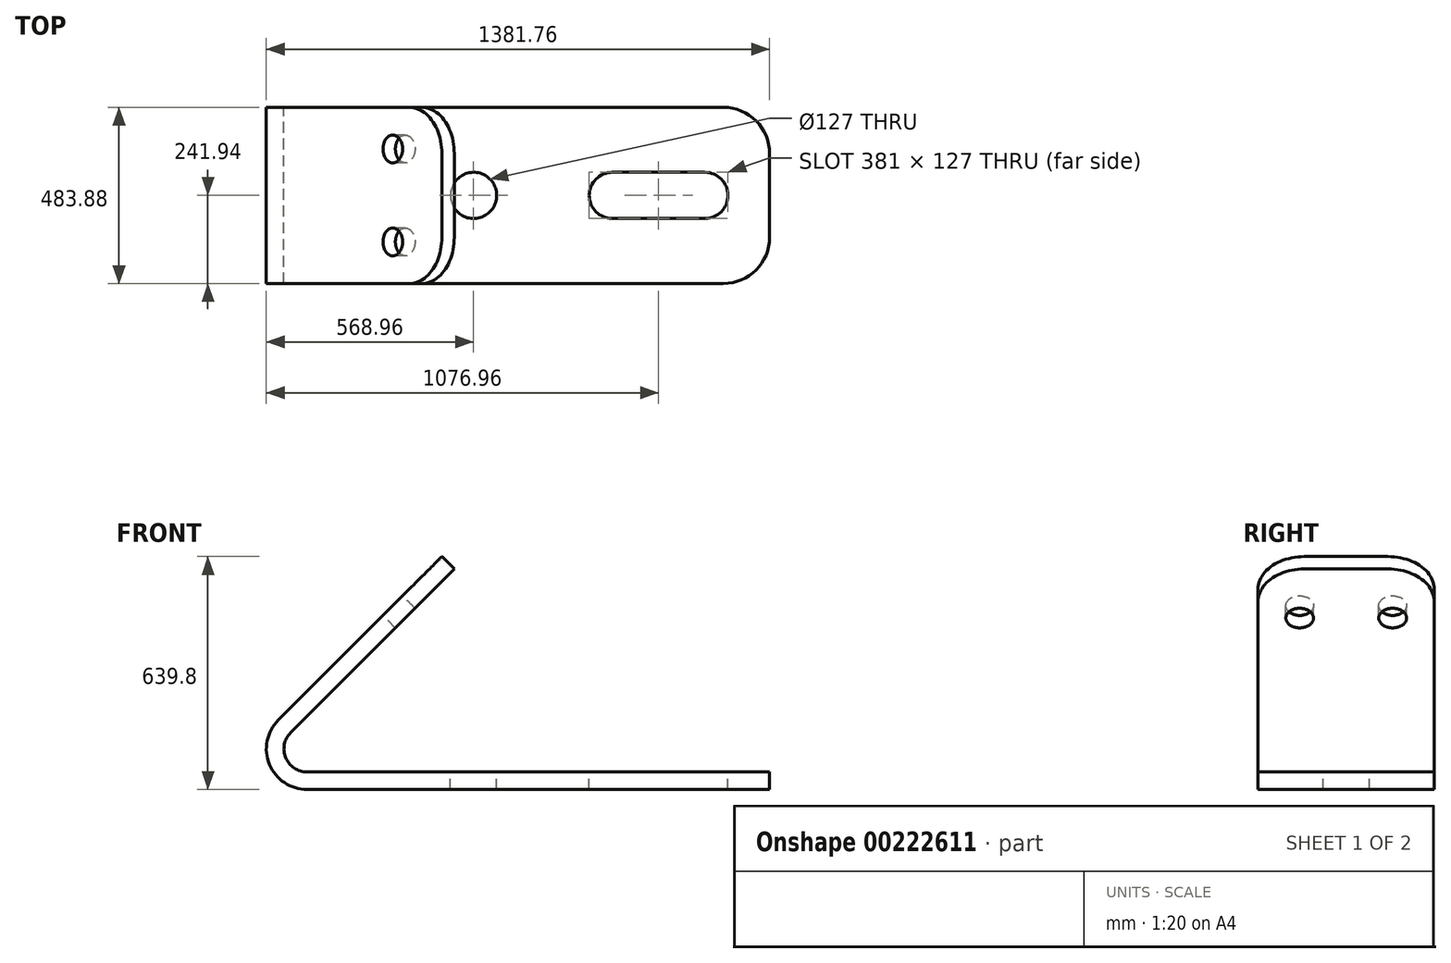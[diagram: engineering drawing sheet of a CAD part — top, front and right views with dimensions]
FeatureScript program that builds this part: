
annotation { "Feature Type Name" : "Feature", "Feature Type Description" : "" }
export const myFeature = defineFeature(function(context is Context, id is Id, definition is map)
    precondition{}
    {
        {
            var Q0;
            Q0=qCreatedBy(makeId("Front.planeOp"),FACE);
            var sketch = newSketch(context, id + "F0", { "sketchPlane" : qUnion([Q0])});
            skLineSegment(sketch, "E0", {"start": v(0, 0) * mm, "end": v(1270, 0) * mm});
            skLineSegment(sketch, "E1", {"start": v(1270, 0) * mm, "end": v(1270, 48.26) * mm});
            skLineSegment(sketch, "E2", {"start": v(369.99, 639.8) * mm, "end": v(-79.03, 190.79) * mm});
            skArc(sketch, "E3", {"start": v(-79.03, 190.79) * mm, "mid": v(-103.25, 69) * mm, "end": v(0, 0) * mm});
            skLineSegment(sketch, "E4", {"start": v(369.99, 639.8) * mm, "end": v(404.11, 605.67) * mm});
            skLineSegment(sketch, "E5", {"start": v(404.11, 605.67) * mm, "end": v(-44.9, 156.66) * mm});
            skLineSegment(sketch, "E6", {"start": v(1270, 48.26) * mm, "end": v(0, 48.26) * mm});
            skArc(sketch, "E7", {"start": v(0, 48.26) * mm, "mid": v(-58.67, 87.46) * mm, "end": v(-44.9, 156.66) * mm});
            skSolve(sketch);
        }
        {
            var Q0;
            Q0=makeQuery(id+"F0.imprint","IMPRINT",FACE,{"disambiguationData":[TD([[makeQuery(id+"F0.imprint","IMPRINT",EDGE,{"derivedFrom":sQuery(id+"F0.wireOp",EDGE,"E0")}),1.0]])]});
            extrude(context, id + "F1", {"entities" : qUnion([Q0]), "endBound" : BoundingType.SYMMETRIC, "depth" : 483.87 * mm});
        }
        {
            var Q0;
            Q0=makeQuery(id+"F1.opExtrude","SWEPT_FACE",FACE,{"disambiguationData":[OSD([sQuery(id+"F0.wireOp",EDGE,"E2")])]});
            var sketch = newSketch(context, id + "F2", { "sketchPlane" : qUnion([Q0])});
            skCircle(sketch, "E8", {"center": v(-127.64, 523.53) * mm, "radius": 38.1 * mm});
            skCircle(sketch, "E9", {"center": v(127.64, 523.53) * mm, "radius": 38.1 * mm});
            skSolve(sketch);
        }
        {
            var Q0;
            Q0 = qSketchRegion(id + "F2", true);
            extrude(context, id + "F3", {"entities" : qUnion([Q0]), "operationType" : NewBodyOperationType.REMOVE, "endBound" : BoundingType.UP_TO_NEXT, "oppositeDirection" : true, "depth" : 25.4 * mm});
        }
        {
            var Q0;
            Q0=makeQuery(id+"F1.opExtrude","SWEPT_FACE",FACE,{"disambiguationData":[OSD([sQuery(id+"F0.wireOp",EDGE,"E6")])]});
            var sketch = newSketch(context, id + "F4", { "sketchPlane" : qUnion([Q0])});
            skCircle(sketch, "E10", {"center": v(457.2, 0) * mm, "radius": 63.5 * mm});
            skLineSegment(sketch, "E11.bottom", {"start": v(1092.2, 63.5) * mm, "end": v(838.2, 63.5) * mm});
            skLineSegment(sketch, "E11.top", {"start": v(1092.2, -63.5) * mm, "end": v(838.2, -63.5) * mm});
            skPoint(sketch, "E11.middle", {"position": v(965.2, 0) * mm});
            skArc(sketch, "E12", {"start": v(838.2, 63.5) * mm, "mid": v(774.7, 0) * mm, "end": v(838.2, -63.5) * mm});
            skArc(sketch, "E13", {"start": v(1092.2, -63.5) * mm, "mid": v(1155.7, 0) * mm, "end": v(1092.2, 63.5) * mm});
            skPoint(sketch, "E13.centerSnap0", {"position": v(1155.7, 0) * mm});
            skPoint(sketch, "E14.orphan", {"position": v(774.7, 63.5) * mm});
            skPoint(sketch, "E15.orphan", {"position": v(774.7, -63.5) * mm});
            skPoint(sketch, "E16.orphan", {"position": v(1155.7, 63.5) * mm});
            skPoint(sketch, "E17.orphan", {"position": v(1155.7, -63.5) * mm});
            skSolve(sketch);
        }
        {
            var Q0;
            Q0 = qSketchRegion(id + "F4", true);
            extrude(context, id + "F5", {"entities" : qUnion([Q0]), "operationType" : NewBodyOperationType.REMOVE, "endBound" : BoundingType.THROUGH_ALL, "oppositeDirection" : true, "depth" : 25.4 * mm});
        }
        {
            var Q0;
            Q0=makeQuery(id+"F1.opExtrude","CAP_EDGE",EDGE,{"disambiguationData":[OSD([sQuery(id+"F0.wireOp",EDGE,"E4")])],"isStart":false});
            var Q1;
            Q1=makeQuery(id+"F1.opExtrude","CAP_EDGE",EDGE,{"disambiguationData":[OSD([sQuery(id+"F0.wireOp",EDGE,"E4")])],"isStart":true});
            var Q2;
            Q2=makeQuery(id+"F1.opExtrude","CAP_EDGE",EDGE,{"disambiguationData":[OSD([sQuery(id+"F0.wireOp",EDGE,"E1")])],"isStart":false});
            var Q3;
            Q3=makeQuery(id+"F1.opExtrude","CAP_EDGE",EDGE,{"disambiguationData":[OSD([sQuery(id+"F0.wireOp",EDGE,"E1")])],"isStart":true});
            fillet(context, id + "F6", {"entities" : qUnion([Q0, Q1, Q2, Q3]), "radius" : 127 * mm, "tangentPropagation" : true, "allowEdgeOverflow" : false});
        }
    });
